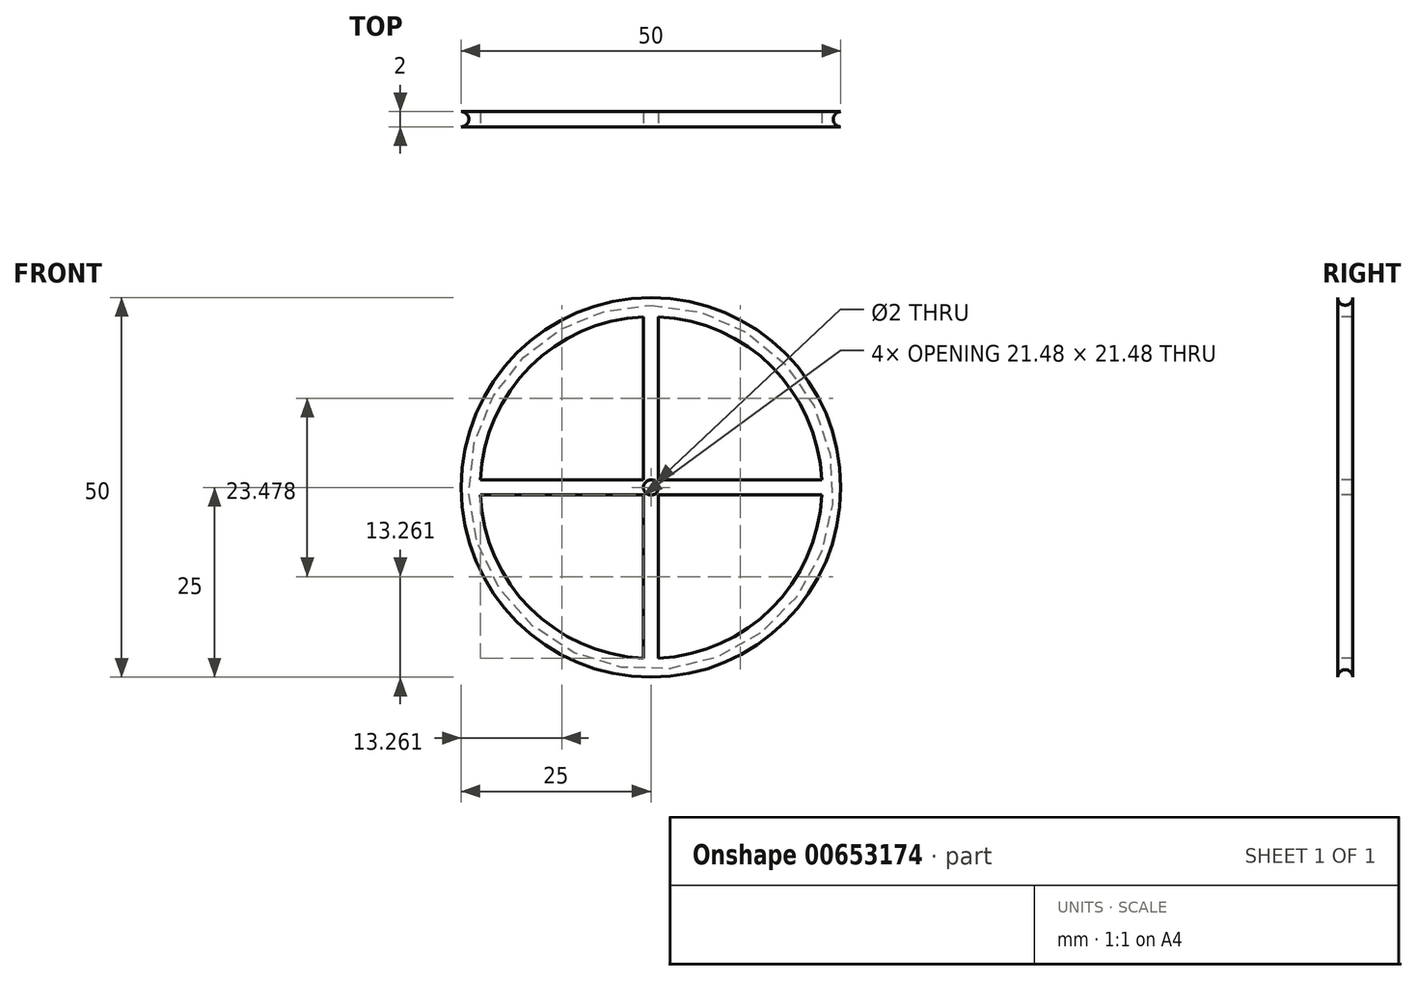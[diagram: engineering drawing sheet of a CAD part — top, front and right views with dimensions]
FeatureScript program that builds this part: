
annotation { "Feature Type Name" : "Feature", "Feature Type Description" : "" }
export const myFeature = defineFeature(function(context is Context, id is Id, definition is map)
    precondition{}
    {
        {
            var Q0;
            Q0=qCreatedBy(makeId("Top.planeOp"),FACE);
            var sketch = newSketch(context, id + "F0", { "sketchPlane" : qUnion([Q0])});
            skLineSegment(sketch, "E0.bottom", {"start": v(0, 0) * mm, "end": v(25, 0) * mm});
            skLineSegment(sketch, "E0.top", {"start": v(0, -2) * mm, "end": v(25, -2) * mm});
            skLineSegment(sketch, "E0.left", {"start": v(0, 0) * mm, "end": v(0, -2) * mm});
            skArc(sketch, "E1", {"start": v(25, 0) * mm, "mid": v(24, -1) * mm, "end": v(25, -2) * mm});
            skSolve(sketch);
        }
        {
            var Q0;
            Q0=makeQuery(id+"F0.imprint","IMPRINT",FACE,{"disambiguationData":[TD([[makeQuery(id+"F0.imprint","IMPRINT",EDGE,{"derivedFrom":sQuery(id+"F0.wireOp",EDGE,"E0.bottom")}),-1.0]])]});
            var Q1;
            Q1=sQuery(id+"F0.wireOp",EDGE,"E0.left");
            revolve(context, id + "F1", {"entities" : qUnion([Q0]), "axis" : qUnion([Q1]), "revolveType" : RevolveType.FULL});
        }
        {
            var Q0;
            Q0=makeQuery(id+"F1.opRevolve","SWEPT_FACE",FACE,{"disambiguationData":[OSD([sQuery(id+"F0.wireOp",EDGE,"E0.top")])]});
            var sketch = newSketch(context, id + "F2", { "sketchPlane" : qUnion([Q0])});
            skCircle(sketch, "E2", {"center": v(0, 0) * mm, "radius": 1 * mm});
            skSolve(sketch);
        }
        {
            var Q0;
            Q0=makeQuery(id+"F2.imprint","IMPRINT",FACE,{"disambiguationData":[TD([[makeQuery(id+"F2.imprint","IMPRINT",EDGE,{"derivedFrom":sQuery(id+"F2.wireOp",EDGE,"E2")}),1.0]])]});
            extrude(context, id + "F3", {"entities" : qUnion([Q0]), "operationType" : NewBodyOperationType.REMOVE, "oppositeDirection" : true, "depth" : 25 * mm, "offsetDistance" : 25 * mm});
        }
        {
            var Q0;
            Q0=makeQuery(id+"F1.opRevolve","SWEPT_FACE",FACE,{"disambiguationData":[OSD([sQuery(id+"F0.wireOp",EDGE,"E0.top")])]});
            var sketch = newSketch(context, id + "F4", { "sketchPlane" : qUnion([Q0])});
            skCircle(sketch, "E3", {"center": v(0, 0) * mm, "radius": 22.5 * mm});
            skLineSegment(sketch, "E4", {"start": v(1, 0) * mm, "end": v(1, 22.48) * mm});
            skLineSegment(sketch, "E5", {"start": v(-1, 0) * mm, "end": v(-1, 22.48) * mm});
            skLineSegment(sketch, "E6", {"start": v(0, 1) * mm, "end": v(22.48, 1) * mm});
            skLineSegment(sketch, "E7", {"start": v(0, -1) * mm, "end": v(22.48, -1) * mm});
            skLineSegment(sketch, "E8", {"start": v(1, 0) * mm, "end": v(1, -22.48) * mm});
            skLineSegment(sketch, "E9", {"start": v(-1, 0) * mm, "end": v(-1, -22.48) * mm});
            skLineSegment(sketch, "E10", {"start": v(0, -1) * mm, "end": v(-22.48, -1) * mm});
            skLineSegment(sketch, "E11", {"start": v(0, 1) * mm, "end": v(-22.48, 1) * mm});
            skSolve(sketch);
        }
        {
            var Q0;
            {var subQ0=sQuery(id+"F4.wireOp",EDGE,"E5");var subQ1=sQuery(id+"F4.wireOp",EDGE,"E3");var subQ2=makeQuery(id+"F4.imprint","INTERSECT",VERTEX,{"derivedFrom":[subQ1,subQ0]});Q0=makeQuery(id+"F4.imprint","IMPRINT",FACE,{"disambiguationData":[TD([[makeQuery(id+"F4.imprint","IMPRINT",EDGE,{"disambiguationData":[TD([[subQ2,-1.0]])],"derivedFrom":subQ1}),1.0]])]});}
            var Q1;
            {var subQ0=sQuery(id+"F4.wireOp",EDGE,"E9");var subQ1=sQuery(id+"F4.wireOp",EDGE,"E3");var subQ2=makeQuery(id+"F4.imprint","INTERSECT",VERTEX,{"derivedFrom":[subQ1,subQ0]});Q1=makeQuery(id+"F4.imprint","IMPRINT",FACE,{"disambiguationData":[TD([[makeQuery(id+"F4.imprint","IMPRINT",EDGE,{"disambiguationData":[TD([[subQ2,1.0]])],"derivedFrom":subQ1}),1.0]])]});}
            var Q2;
            {var subQ0=sQuery(id+"F4.wireOp",EDGE,"E7");var subQ1=sQuery(id+"F4.wireOp",EDGE,"E3");var subQ2=makeQuery(id+"F4.imprint","INTERSECT",VERTEX,{"derivedFrom":[subQ1,subQ0]});Q2=makeQuery(id+"F4.imprint","IMPRINT",FACE,{"disambiguationData":[TD([[makeQuery(id+"F4.imprint","IMPRINT",EDGE,{"disambiguationData":[TD([[subQ2,1.0]])],"derivedFrom":subQ1}),1.0]])]});}
            var Q3;
            {var subQ0=sQuery(id+"F4.wireOp",EDGE,"E4");var subQ1=sQuery(id+"F4.wireOp",EDGE,"E3");var subQ2=makeQuery(id+"F4.imprint","INTERSECT",VERTEX,{"derivedFrom":[subQ1,subQ0]});Q3=makeQuery(id+"F4.imprint","IMPRINT",FACE,{"disambiguationData":[TD([[makeQuery(id+"F4.imprint","IMPRINT",EDGE,{"disambiguationData":[TD([[subQ2,1.0]])],"derivedFrom":subQ1}),1.0]])]});}
            extrude(context, id + "F5", {"entities" : qUnion([Q0, Q1, Q2, Q3]), "operationType" : NewBodyOperationType.REMOVE, "oppositeDirection" : true, "depth" : 25 * mm, "offsetDistance" : 25 * mm});
        }
    });
